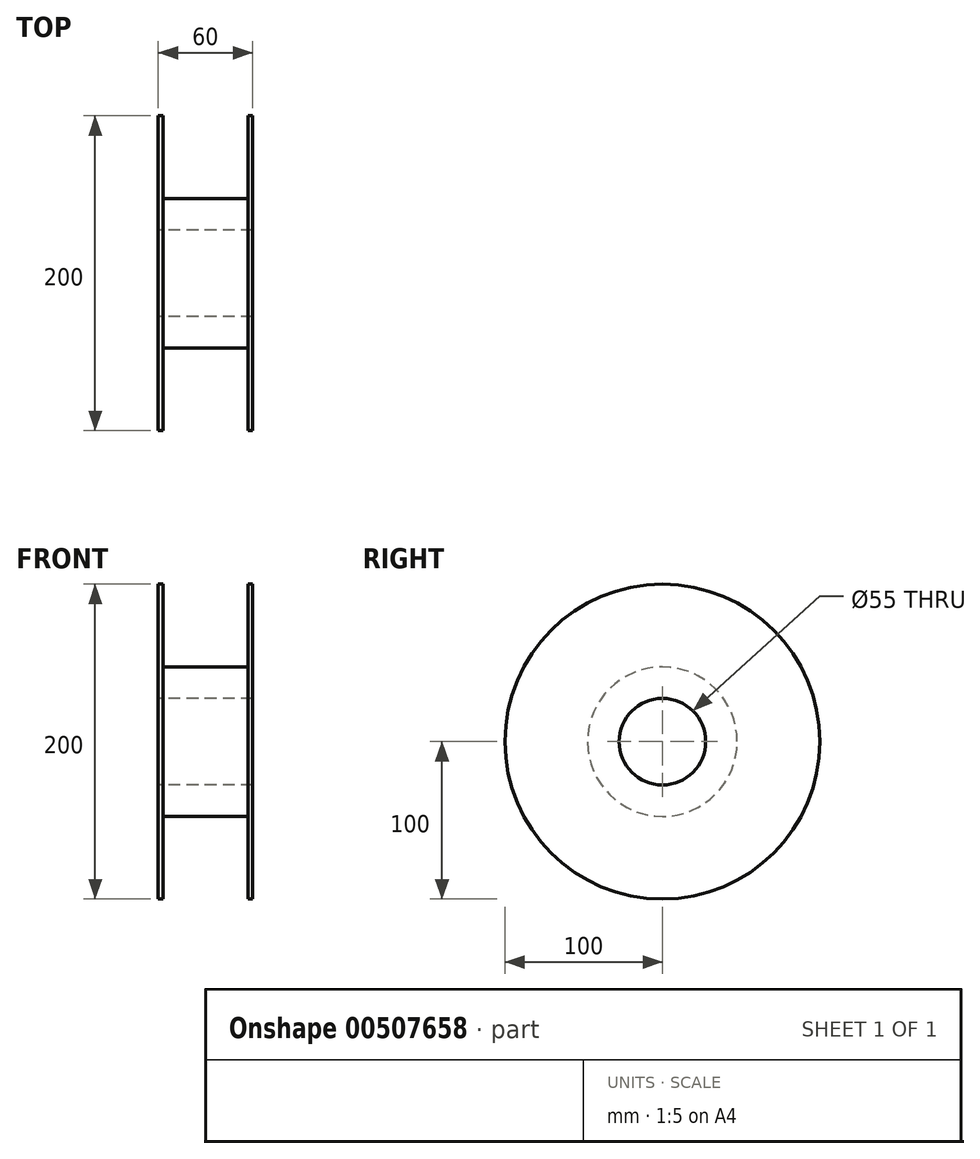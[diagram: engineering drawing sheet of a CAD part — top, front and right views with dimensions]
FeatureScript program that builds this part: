
annotation { "Feature Type Name" : "Feature", "Feature Type Description" : "" }
export const myFeature = defineFeature(function(context is Context, id is Id, definition is map)
    precondition{}
    {
        {
            var Q0;
            Q0=qCreatedBy(makeId("Right.planeOp"),FACE);
            var sketch = newSketch(context, id + "F0", { "sketchPlane" : qUnion([Q0])});
            skCircle(sketch, "E0", {"center": v(0, 0) * mm, "radius": 47.5 * mm});
            skCircle(sketch, "E1", {"center": v(0, 0) * mm, "radius": 27.5 * mm});
            skSolve(sketch);
        }
        {
            var Q0;
            Q0=makeQuery(id+"F0.imprint","IMPRINT",FACE,{"disambiguationData":[TD([[makeQuery(id+"F0.imprint","IMPRINT",EDGE,{"derivedFrom":sQuery(id+"F0.wireOp",EDGE,"E0")}),1.0]])]});
            extrude(context, id + "F1", {"entities" : qUnion([Q0]), "depth" : 30 * mm, "offsetDistance" : 25 * mm});
        }
        {
            var Q0;
            Q0=makeQuery(id+"F1.opExtrude","CAP_FACE",FACE,{"disambiguationData":[OSD([sQuery(id+"F0.wireOp",EDGE,"E0"),sQuery(id+"F0.wireOp",EDGE,"E1")])],"isStart":false});
            var sketch = newSketch(context, id + "F2", { "sketchPlane" : qUnion([Q0])});
            skCircle(sketch, "E2", {"center": v(0, 0) * mm, "radius": 100 * mm});
            skCircle(sketch, "E3.0", {"center": v(0, 0) * mm, "radius": 47.5 * mm});
            skSolve(sketch);
        }
        {
            var Q0;
            Q0=makeQuery(id+"F2.imprint","IMPRINT",FACE,{"disambiguationData":[TD([[makeQuery(id+"F2.imprint","IMPRINT",EDGE,{"derivedFrom":sQuery(id+"F2.wireOp",EDGE,"E2")}),1.0]])]});
            extrude(context, id + "F3", {"entities" : qUnion([Q0]), "operationType" : NewBodyOperationType.ADD, "oppositeDirection" : true, "depth" : 3 * mm});
        }
        {
            var Q0;
            Q0=makeQuery(id+"F1.opExtrude","SWEPT_BODY",BODY,{"disambiguationData":[OSD([sQuery(id+"F0.wireOp",EDGE,"E0"),sQuery(id+"F0.wireOp",EDGE,"E1")])]});
            var Q1;
            Q1=makeQuery(id+"F1.opExtrude","CAP_FACE",FACE,{"disambiguationData":[OSD([sQuery(id+"F0.wireOp",EDGE,"E0"),sQuery(id+"F0.wireOp",EDGE,"E1")])],"isStart":true});
            mirror(context, id + "F4", {"operationType" : NewBodyOperationType.ADD, "entities" : qUnion([Q0]), "mirrorPlane" : qUnion([Q1])});
        }
    });
